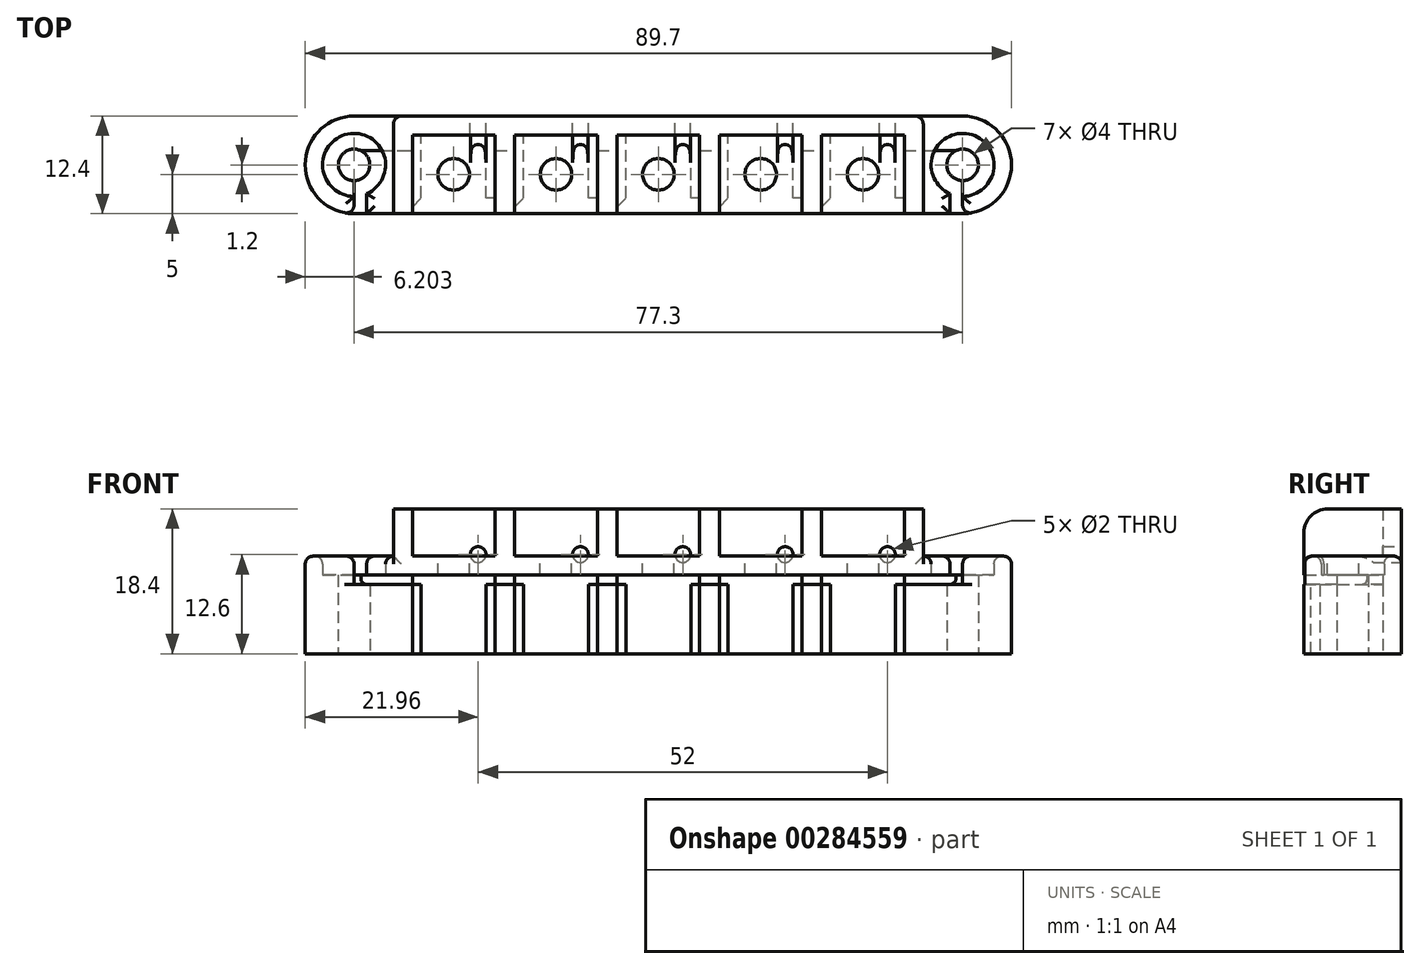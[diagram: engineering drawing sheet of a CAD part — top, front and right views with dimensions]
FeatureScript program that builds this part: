
annotation { "Feature Type Name" : "Feature", "Feature Type Description" : "" }
export const myFeature = defineFeature(function(context is Context, id is Id, definition is map)
    precondition{}
    {
        {
            var Q0;
            Q0=qCreatedBy(makeId("Top.planeOp"),FACE);
            var sketch = newSketch(context, id + "F0", { "sketchPlane" : qUnion([Q0])});
            skLineSegment(sketch, "E0.bottom", {"start": v(-33.77, 0) * mm, "end": v(-23.27, 0) * mm, "construction": true});
            skLineSegment(sketch, "E0.left", {"start": v(-33.77, 0) * mm, "end": v(-33.77, -10) * mm, "construction": true});
            skLineSegment(sketch, "E0.right", {"start": v(-23.27, 0) * mm, "end": v(-23.27, -10) * mm, "construction": true});
            skLineSegment(sketch, "E1.top", {"start": v(-23.27, -10) * mm, "end": v(-20.87, -10) * mm, "construction": true});
            skLineSegment(sketch, "E2.bottom", {"start": v(-36.17, 2.4) * mm, "end": v(31.13, 2.4) * mm, "construction": true});
            skLineSegment(sketch, "E2.left", {"start": v(-36.17, 2.4) * mm, "end": v(-36.17, -10) * mm, "construction": true});
            skArc(sketch, "E3", {"start": v(-41.17, 2.4) * mm, "mid": v(-47.37, -3.8) * mm, "end": v(-41.17, -10) * mm, "construction": true});
            skArc(sketch, "E4", {"start": v(36.13, -10) * mm, "mid": v(42.33, -3.8) * mm, "end": v(36.13, 2.4) * mm, "construction": true});
            skLineSegment(sketch, "E5", {"start": v(-41.17, -10) * mm, "end": v(-36.17, -10) * mm, "construction": true});
            skLineSegment(sketch, "E6", {"start": v(-41.17, 2.4) * mm, "end": v(-36.17, 2.4) * mm, "construction": true});
            skLineSegment(sketch, "E7", {"start": v(-55.27, -5) * mm, "end": v(51.36, -5) * mm, "construction": true});
            skLineSegment(sketch, "E8", {"start": v(-36.17, -10) * mm, "end": v(-33.77, -10) * mm, "construction": true});
            skLineSegment(sketch, "E9.1.0.0", {"start": v(-20.77, 0) * mm, "end": v(-20.77, -10) * mm, "construction": true});
            skLineSegment(sketch, "E9.1.0.1", {"start": v(-20.77, 0) * mm, "end": v(-10.27, 0) * mm, "construction": true});
            skLineSegment(sketch, "E9.1.0.2", {"start": v(-10.27, 0) * mm, "end": v(-10.27, -10) * mm, "construction": true});
            skLineSegment(sketch, "E9.1.0.3", {"start": v(-10.27, -10) * mm, "end": v(-7.87, -10) * mm, "construction": true});
            skLineSegment(sketch, "E9.2.0.0", {"start": v(-7.77, 0) * mm, "end": v(-7.77, -10) * mm, "construction": true});
            skLineSegment(sketch, "E9.2.0.1", {"start": v(-7.77, 0) * mm, "end": v(2.73, 0) * mm, "construction": true});
            skLineSegment(sketch, "E9.2.0.2", {"start": v(2.73, 0) * mm, "end": v(2.73, -10) * mm, "construction": true});
            skLineSegment(sketch, "E9.2.0.3", {"start": v(2.73, -10) * mm, "end": v(5.13, -10) * mm, "construction": true});
            skLineSegment(sketch, "E9.3.0.0", {"start": v(5.23, 0) * mm, "end": v(5.23, -10) * mm, "construction": true});
            skLineSegment(sketch, "E9.3.0.1", {"start": v(5.23, 0) * mm, "end": v(15.73, 0) * mm, "construction": true});
            skLineSegment(sketch, "E9.3.0.2", {"start": v(15.73, 0) * mm, "end": v(15.73, -10) * mm, "construction": true});
            skLineSegment(sketch, "E9.3.0.3", {"start": v(15.73, -10) * mm, "end": v(18.13, -10) * mm, "construction": true});
            skLineSegment(sketch, "E9.4.0.0", {"start": v(18.23, 0) * mm, "end": v(18.23, -10) * mm, "construction": true});
            skLineSegment(sketch, "E9.4.0.1", {"start": v(18.23, 0) * mm, "end": v(28.73, 0) * mm, "construction": true});
            skLineSegment(sketch, "E9.4.0.2", {"start": v(28.73, 0) * mm, "end": v(28.73, -10) * mm, "construction": true});
            skLineSegment(sketch, "E9.4.0.3", {"start": v(28.73, -10) * mm, "end": v(31.13, -10) * mm, "construction": true});
            skLineSegment(sketch, "E9.direction1", {"start": v(-33.77, -10) * mm, "end": v(-20.77, -10) * mm, "construction": true});
            skLineSegment(sketch, "E10", {"start": v(31.13, -10) * mm, "end": v(31.13, 2.4) * mm, "construction": true});
            skLineSegment(sketch, "E11", {"start": v(31.13, 2.4) * mm, "end": v(36.13, 2.4) * mm, "construction": true});
            skLineSegment(sketch, "E12", {"start": v(36.13, -10) * mm, "end": v(31.13, -10) * mm, "construction": true});
            skSolve(sketch);
        }
        {
            var Q0;
            Q0=qCreatedBy(makeId("Top.planeOp"),FACE);
            var sketch = newSketch(context, id + "F1", { "sketchPlane" : qUnion([Q0])});
            skLineSegment(sketch, "E13", {"start": v(-36.17, -10) * mm, "end": v(-33.77, -10) * mm});
            skLineSegment(sketch, "E14", {"start": v(-33.77, -10) * mm, "end": v(-33.77, 0) * mm});
            skLineSegment(sketch, "E15", {"start": v(-33.77, 0) * mm, "end": v(-23.27, 0) * mm});
            skLineSegment(sketch, "E16", {"start": v(-23.27, 0) * mm, "end": v(-23.27, -10) * mm});
            skLineSegment(sketch, "E17.1.0.0", {"start": v(-10.27, 0) * mm, "end": v(-10.27, -10) * mm});
            skLineSegment(sketch, "E17.1.0.1", {"start": v(-20.77, -10) * mm, "end": v(-20.77, 0) * mm});
            skLineSegment(sketch, "E17.1.0.2", {"start": v(-20.77, 0) * mm, "end": v(-10.27, 0) * mm});
            skLineSegment(sketch, "E17.1.0.3", {"start": v(-23.27, -10) * mm, "end": v(-20.77, -10) * mm});
            skLineSegment(sketch, "E17.2.0.0", {"start": v(2.73, 0) * mm, "end": v(2.73, -10) * mm});
            skLineSegment(sketch, "E17.2.0.1", {"start": v(-7.77, -10) * mm, "end": v(-7.77, 0) * mm});
            skLineSegment(sketch, "E17.2.0.2", {"start": v(-7.77, 0) * mm, "end": v(2.73, 0) * mm});
            skLineSegment(sketch, "E17.2.0.3", {"start": v(-10.27, -10) * mm, "end": v(-7.77, -10) * mm});
            skLineSegment(sketch, "E17.3.0.0", {"start": v(15.73, 0) * mm, "end": v(15.73, -10) * mm});
            skLineSegment(sketch, "E17.3.0.1", {"start": v(5.23, -10) * mm, "end": v(5.23, 0) * mm});
            skLineSegment(sketch, "E17.3.0.2", {"start": v(5.23, 0) * mm, "end": v(15.73, 0) * mm});
            skLineSegment(sketch, "E17.3.0.3", {"start": v(2.73, -10) * mm, "end": v(5.23, -10) * mm});
            skLineSegment(sketch, "E17.4.0.0", {"start": v(28.73, 0) * mm, "end": v(28.73, -10) * mm});
            skLineSegment(sketch, "E17.4.0.1", {"start": v(18.23, -10) * mm, "end": v(18.23, 0) * mm});
            skLineSegment(sketch, "E17.4.0.2", {"start": v(18.23, 0) * mm, "end": v(28.73, 0) * mm});
            skLineSegment(sketch, "E17.4.0.3", {"start": v(15.73, -10) * mm, "end": v(18.23, -10) * mm});
            skLineSegment(sketch, "E18", {"start": v(-36.17, -10) * mm, "end": v(-36.17, 2.4) * mm});
            skLineSegment(sketch, "E19", {"start": v(-36.17, 2.4) * mm, "end": v(31.13, 2.4) * mm});
            skLineSegment(sketch, "E20", {"start": v(31.13, 2.4) * mm, "end": v(31.13, -10) * mm});
            skLineSegment(sketch, "E21", {"start": v(31.13, -10) * mm, "end": v(28.73, -10) * mm});
            skSolve(sketch);
        }
        {
            var Q0;
            Q0 = qSketchRegion(id + "F1", true);
            extrude(context, id + "F2", {"entities" : qUnion([Q0]), "depth" : 10 * mm});
        }
        {
            var Q0;
            Q0=qCreatedBy(makeId("Top.planeOp"),FACE);
            var sketch = newSketch(context, id + "F3", { "sketchPlane" : qUnion([Q0])});
            skArc(sketch, "E22", {"start": v(-41.17, 2.4) * mm, "mid": v(-47.37, -3.8) * mm, "end": v(-41.17, -10) * mm});
            skLineSegment(sketch, "E23.bottom", {"start": v(-36.17, 2.4) * mm, "end": v(-41.17, 2.4) * mm});
            skLineSegment(sketch, "E23.top", {"start": v(-36.17, -10) * mm, "end": v(-41.17, -10) * mm});
            skLineSegment(sketch, "E24.bottom", {"start": v(36.13, 2.4) * mm, "end": v(31.13, 2.4) * mm});
            skLineSegment(sketch, "E24.top", {"start": v(36.13, -10) * mm, "end": v(31.13, -10) * mm});
            skLineSegment(sketch, "E24.right", {"start": v(31.13, 2.4) * mm, "end": v(31.13, -10) * mm});
            skArc(sketch, "E25", {"start": v(36.13, -10) * mm, "mid": v(42.33, -3.8) * mm, "end": v(36.13, 2.4) * mm});
            skCircle(sketch, "E26", {"center": v(36.13, -3.8) * mm, "radius": 2 * mm});
            skCircle(sketch, "E27", {"center": v(-41.17, -3.8) * mm, "radius": 2 * mm});
            skLineSegment(sketch, "E28", {"start": v(-36.17, 2.4) * mm, "end": v(-36.17, -10) * mm});
            skSolve(sketch);
        }
        {
            var Q0;
            Q0 = qSketchRegion(id + "F3", true);
            extrude(context, id + "F4", {"entities" : qUnion([Q0]), "operationType" : NewBodyOperationType.ADD, "depth" : 10 * mm});
        }
        {
            var Q0;
            Q0=makeQuery(id+"F2.opExtrude","SWEPT_FACE",FACE,{"disambiguationData":[OSD([sQuery(id+"F1.wireOp",EDGE,"E17.2.0.3")])]});
            var sketch = newSketch(context, id + "F5", { "sketchPlane" : qUnion([Q0])});
            skPoint(sketch, "E29.oppositeSnap0", {"position": v(16.83, 8.8) * mm});
            skLineSegment(sketch, "E29.bottom", {"start": v(-41.17, 10) * mm, "end": v(36.13, 10) * mm});
            skLineSegment(sketch, "E29.top", {"start": v(-41.17, 8.8) * mm, "end": v(36.13, 8.8) * mm});
            skLineSegment(sketch, "E29.left", {"start": v(-41.17, 10) * mm, "end": v(-41.17, 8.8) * mm});
            skLineSegment(sketch, "E29.right", {"start": v(36.13, 10) * mm, "end": v(36.13, 8.8) * mm});
            skSolve(sketch);
        }
        {
            var Q0;
            Q0 = qSketchRegion(id + "F5", true);
            extrude(context, id + "F6", {"entities" : qUnion([Q0]), "operationType" : NewBodyOperationType.REMOVE, "oppositeDirection" : true, "depth" : 8 * mm});
        }
        {
            var Q0;
            Q0=makeQuery(id+"F4.boolean.opBoolean","MERGE",FACE,{"derivedFrom":[makeQuery(id+"FwgUjB52n0EN0py_0.opExtrude","CAP_FACE",FACE,{"disambiguationData":[OSD([sQuery(id+"F1.wireOp",EDGE,"fT5GCNOj-Di1p-hgey-o5If-u0ZHMEbWG8jb.bottom"),sQuery(id+"F1.wireOp",EDGE,"fT5GCNOj-Di1p-hgey-o5If-u0ZHMEbWG8jb.left"),sQuery(id+"F1.wireOp",EDGE,"fT5GCNOj-Di1p-hgey-o5If-u0ZHMEbWG8jb.right"),sQuery(id+"F1.wireOp",EDGE,"4aupWsoh-EStk-4eZo-ruS9-NkXySoXvfakK"),sQuery(id+"F1.wireOp",EDGE,"e8ce3505-5f8b-4699-837b-7b2c080ba128.1.0.0"),sQuery(id+"F1.wireOp",EDGE,"e8ce3505-5f8b-4699-837b-7b2c080ba128.1.0.1"),sQuery(id+"F1.wireOp",EDGE,"e8ce3505-5f8b-4699-837b-7b2c080ba128.1.0.2"),sQuery(id+"F1.wireOp",EDGE,"e8ce3505-5f8b-4699-837b-7b2c080ba128.1.0.3"),sQuery(id+"F1.wireOp",EDGE,"e8ce3505-5f8b-4699-837b-7b2c080ba128.2.0.0"),sQuery(id+"F1.wireOp",EDGE,"e8ce3505-5f8b-4699-837b-7b2c080ba128.2.0.1"),sQuery(id+"F1.wireOp",EDGE,"e8ce3505-5f8b-4699-837b-7b2c080ba128.2.0.2"),sQuery(id+"F1.wireOp",EDGE,"e8ce3505-5f8b-4699-837b-7b2c080ba128.2.0.3"),sQuery(id+"F1.wireOp",EDGE,"e8ce3505-5f8b-4699-837b-7b2c080ba128.3.0.0"),sQuery(id+"F1.wireOp",EDGE,"e8ce3505-5f8b-4699-837b-7b2c080ba128.3.0.1"),sQuery(id+"F1.wireOp",EDGE,"e8ce3505-5f8b-4699-837b-7b2c080ba128.3.0.2"),sQuery(id+"F1.wireOp",EDGE,"e8ce3505-5f8b-4699-837b-7b2c080ba128.3.0.3"),sQuery(id+"F1.wireOp",EDGE,"e8ce3505-5f8b-4699-837b-7b2c080ba128.4.0.0"),sQuery(id+"F1.wireOp",EDGE,"e8ce3505-5f8b-4699-837b-7b2c080ba128.4.0.1"),sQuery(id+"F1.wireOp",EDGE,"e8ce3505-5f8b-4699-837b-7b2c080ba128.4.0.2"),sQuery(id+"F1.wireOp",EDGE,"e8ce3505-5f8b-4699-837b-7b2c080ba128.4.0.3"),sQuery(id+"F1.wireOp",EDGE,"e8ce3505-5f8b-4699-837b-7b2c080ba128.5.0.0"),sQuery(id+"F1.wireOp",EDGE,"e8ce3505-5f8b-4699-837b-7b2c080ba128.5.0.1"),sQuery(id+"F1.wireOp",EDGE,"e8ce3505-5f8b-4699-837b-7b2c080ba128.5.0.2"),sQuery(id+"F1.wireOp",EDGE,"e8ce3505-5f8b-4699-837b-7b2c080ba128.5.0.3"),sQuery(id+"F1.wireOp",EDGE,"WsZVMAvk-gSrm-D8FK-Weo4-wgcM3uc7j39G"),sQuery(id+"F1.wireOp",EDGE,"UKXqcqMu-vQly-xDY7-aWyL-ivSJE3wOXlFD"),sQuery(id+"F1.wireOp",EDGE,"qiBo0CbL-PMXg-gfnk-IXnX-IWupUi0J8d6I"),sQuery(id+"F1.wireOp",EDGE,"uGecGJv5-VCCF-BD4v-ZbDO-07ZKYqrsvqIm")])],"isStart":false}),makeQuery(id+"F4.opExtrude","CAP_FACE",FACE,{"disambiguationData":[OSD([sQuery(id+"F3.wireOp",EDGE,"E22"),sQuery(id+"F3.wireOp",EDGE,"E23.bottom"),sQuery(id+"F3.wireOp",EDGE,"E23.top"),sQuery(id+"F3.wireOp",EDGE,"E27"),sQuery(id+"F3.wireOp",EDGE,"E28")])],"isStart":false}),makeQuery(id+"F4.opExtrude","CAP_FACE",FACE,{"disambiguationData":[OSD([sQuery(id+"F3.wireOp",EDGE,"E24.bottom"),sQuery(id+"F3.wireOp",EDGE,"E24.top"),sQuery(id+"F3.wireOp",EDGE,"E24.right"),sQuery(id+"F3.wireOp",EDGE,"E25"),sQuery(id+"F3.wireOp",EDGE,"E26")])],"isStart":false})]});
            var sketch = newSketch(context, id + "F7", { "sketchPlane" : qUnion([Q0])});
            skLineSegment(sketch, "E30.bottom", {"start": v(-36.17, 2.4) * mm, "end": v(29.83, 2.4) * mm});
            skLineSegment(sketch, "E30.top", {"start": v(-36.17, -10) * mm, "end": v(29.83, -10) * mm});
            skArc(sketch, "E31", {"start": v(-41.17, 2.4) * mm, "mid": v(-47.37, -3.8) * mm, "end": v(-41.17, -10) * mm});
            skLineSegment(sketch, "E32.bottom", {"start": v(-36.17, 2.4) * mm, "end": v(-41.17, 2.4) * mm});
            skLineSegment(sketch, "E32.top", {"start": v(-36.17, -10) * mm, "end": v(-41.17, -10) * mm});
            skArc(sketch, "E33", {"start": v(36.13, -10) * mm, "mid": v(42.33, -3.8) * mm, "end": v(36.13, 2.4) * mm});
            skLineSegment(sketch, "E34.bottom", {"start": v(29.83, 2.4) * mm, "end": v(36.13, 2.4) * mm});
            skLineSegment(sketch, "E34.top", {"start": v(29.83, -10) * mm, "end": v(36.13, -10) * mm});
            skLineSegment(sketch, "E34.right", {"start": v(36.13, 2.4) * mm, "end": v(36.13, -10) * mm});
            skSolve(sketch);
        }
        {
            var Q0;
            Q0 = qSketchRegion(id + "F7", true);
            extrude(context, id + "F8", {"entities" : qUnion([Q0]), "operationType" : NewBodyOperationType.ADD, "depth" : 2.4 * mm});
        }
        {
            var Q0;
            Q0=makeQuery(id+"F8.opExtrude","CAP_FACE",FACE,{"disambiguationData":[OSD([sQuery(id+"F7.wireOp",EDGE,"E30.bottom"),sQuery(id+"F7.wireOp",EDGE,"E30.top"),sQuery(id+"F7.wireOp",EDGE,"E31"),sQuery(id+"F7.wireOp",EDGE,"E32.bottom"),sQuery(id+"F7.wireOp",EDGE,"E32.top"),sQuery(id+"F7.wireOp",EDGE,"E33"),sQuery(id+"F7.wireOp",EDGE,"E34.bottom"),sQuery(id+"F7.wireOp",EDGE,"E34.top")])],"isStart":true});
            var sketch = newSketch(context, id + "F9", { "sketchPlane" : qUnion([Q0])});
            skArc(sketch, "E35", {"start": v(-41.17, 7.8) * mm, "mid": v(-41.98, -0.12) * mm, "end": v(-39.57, 7.47) * mm});
            skArc(sketch, "E36", {"start": v(34.53, 7.47) * mm, "mid": v(36.95, -0.12) * mm, "end": v(36.13, 7.8) * mm});
            skLineSegment(sketch, "E37.bottom", {"start": v(-41.17, 10) * mm, "end": v(-39.57, 10) * mm});
            skLineSegment(sketch, "E37.left", {"start": v(-41.17, 10) * mm, "end": v(-41.17, 7.8) * mm});
            skLineSegment(sketch, "E37.right", {"start": v(-39.57, 10) * mm, "end": v(-39.57, 7.47) * mm});
            skLineSegment(sketch, "E38.bottom", {"start": v(36.13, 10) * mm, "end": v(34.53, 10) * mm});
            skLineSegment(sketch, "E38.left", {"start": v(36.13, 10) * mm, "end": v(36.13, 7.8) * mm});
            skLineSegment(sketch, "E38.right", {"start": v(34.53, 10) * mm, "end": v(34.53, 7.47) * mm});
            skSolve(sketch);
        }
        {
            var Q0;
            Q0 = qSketchRegion(id + "F9", true);
            extrude(context, id + "F10", {"entities" : qUnion([Q0]), "operationType" : NewBodyOperationType.REMOVE, "oppositeDirection" : true, "depth" : 5 * mm});
        }
        {
            var Q0;
            Q0=makeQuery(id+"F8.opExtrude","CAP_FACE",FACE,{"disambiguationData":[OSD([sQuery(id+"F7.wireOp",EDGE,"E30.bottom"),sQuery(id+"F7.wireOp",EDGE,"E30.top"),sQuery(id+"F7.wireOp",EDGE,"E31"),sQuery(id+"F7.wireOp",EDGE,"E32.bottom"),sQuery(id+"F7.wireOp",EDGE,"E32.top"),sQuery(id+"F7.wireOp",EDGE,"E33"),sQuery(id+"F7.wireOp",EDGE,"E34.bottom"),sQuery(id+"F7.wireOp",EDGE,"E34.top")])],"isStart":false});
            var sketch = newSketch(context, id + "F11", { "sketchPlane" : qUnion([Q0])});
            skCircle(sketch, "E39", {"center": v(-28.52, -5) * mm, "radius": 2 * mm});
            skCircle(sketch, "E40.1.0.0", {"center": v(-15.52, -5) * mm, "radius": 2 * mm});
            skCircle(sketch, "E40.2.0.0", {"center": v(-2.52, -5) * mm, "radius": 2 * mm});
            skCircle(sketch, "E40.3.0.0", {"center": v(10.48, -5) * mm, "radius": 2 * mm});
            skCircle(sketch, "E40.4.0.0", {"center": v(23.48, -5) * mm, "radius": 2 * mm});
            skLineSegment(sketch, "E40.direction1", {"start": v(-28.52, -5) * mm, "end": v(-15.52, -5) * mm, "construction": true});
            skSolve(sketch);
        }
        {
            var Q0;
            Q0 = qSketchRegion(id + "F11", true);
            var Q1;
            Q1=makeQuery(id+"F8.opExtrude","CAP_FACE",FACE,{"disambiguationData":[OSD([sQuery(id+"F7.wireOp",EDGE,"E30.bottom"),sQuery(id+"F7.wireOp",EDGE,"E30.top"),sQuery(id+"F7.wireOp",EDGE,"E31"),sQuery(id+"F7.wireOp",EDGE,"E32.bottom"),sQuery(id+"F7.wireOp",EDGE,"E32.top"),sQuery(id+"F7.wireOp",EDGE,"E33"),sQuery(id+"F7.wireOp",EDGE,"E34.bottom"),sQuery(id+"F7.wireOp",EDGE,"E34.top")])],"isStart":true});
            extrude(context, id + "F12", {"entities" : qUnion([Q0]), "operationType" : NewBodyOperationType.REMOVE, "endBound" : BoundingType.UP_TO_SURFACE, "oppositeDirection" : true, "endBoundEntityFace" : qUnion([Q1]), "depth" : 25 * mm});
        }
        {
            var Q0;
            Q0=makeQuery(id+"F8.opExtrude","CAP_FACE",FACE,{"disambiguationData":[OSD([sQuery(id+"F7.wireOp",EDGE,"E30.bottom"),sQuery(id+"F7.wireOp",EDGE,"E30.top"),sQuery(id+"F7.wireOp",EDGE,"E31"),sQuery(id+"F7.wireOp",EDGE,"E32.bottom"),sQuery(id+"F7.wireOp",EDGE,"E32.top"),sQuery(id+"F7.wireOp",EDGE,"E33"),sQuery(id+"F7.wireOp",EDGE,"E34.bottom"),sQuery(id+"F7.wireOp",EDGE,"E34.top")])],"isStart":false});
            var sketch = newSketch(context, id + "F13", { "sketchPlane" : qUnion([Q0])});
            skLineSegment(sketch, "E41.left", {"start": v(-33.77, 0) * mm, "end": v(-33.77, -10) * mm});
            skLineSegment(sketch, "E42", {"start": v(-33.77, -10) * mm, "end": v(-36.17, -10) * mm});
            skLineSegment(sketch, "E43", {"start": v(31.13, 2.4) * mm, "end": v(-36.17, 2.4) * mm});
            skLineSegment(sketch, "E44", {"start": v(-36.17, 2.4) * mm, "end": v(-36.17, -10) * mm});
            skLineSegment(sketch, "E45", {"start": v(-33.77, 0) * mm, "end": v(-23.27, 0) * mm});
            skLineSegment(sketch, "E46", {"start": v(-23.27, 0) * mm, "end": v(-23.27, -10) * mm});
            skLineSegment(sketch, "E47.1.0.0", {"start": v(-20.77, -10) * mm, "end": v(-23.27, -10) * mm});
            skLineSegment(sketch, "E47.1.0.1", {"start": v(-20.77, 0) * mm, "end": v(-20.77, -10) * mm});
            skLineSegment(sketch, "E47.1.0.2", {"start": v(-20.77, 0) * mm, "end": v(-10.27, 0) * mm});
            skLineSegment(sketch, "E47.1.0.3", {"start": v(-10.27, 0) * mm, "end": v(-10.27, -10) * mm});
            skLineSegment(sketch, "E47.2.0.0", {"start": v(-7.77, -10) * mm, "end": v(-10.27, -10) * mm});
            skLineSegment(sketch, "E47.2.0.1", {"start": v(-7.77, 0) * mm, "end": v(-7.77, -10) * mm});
            skLineSegment(sketch, "E47.2.0.2", {"start": v(-7.77, 0) * mm, "end": v(2.73, 0) * mm});
            skLineSegment(sketch, "E47.2.0.3", {"start": v(2.73, 0) * mm, "end": v(2.73, -10) * mm});
            skLineSegment(sketch, "E47.3.0.0", {"start": v(5.23, -10) * mm, "end": v(2.73, -10) * mm});
            skLineSegment(sketch, "E47.3.0.1", {"start": v(5.23, 0) * mm, "end": v(5.23, -10) * mm});
            skLineSegment(sketch, "E47.3.0.2", {"start": v(5.23, 0) * mm, "end": v(15.73, 0) * mm});
            skLineSegment(sketch, "E47.3.0.3", {"start": v(15.73, 0) * mm, "end": v(15.73, -10) * mm});
            skLineSegment(sketch, "E47.4.0.0", {"start": v(18.23, -10) * mm, "end": v(15.73, -10) * mm});
            skLineSegment(sketch, "E47.4.0.1", {"start": v(18.23, 0) * mm, "end": v(18.23, -10) * mm});
            skLineSegment(sketch, "E47.4.0.2", {"start": v(18.23, 0) * mm, "end": v(28.73, 0) * mm});
            skLineSegment(sketch, "E47.4.0.3", {"start": v(28.73, 0) * mm, "end": v(28.73, -10) * mm});
            skLineSegment(sketch, "E48", {"start": v(28.73, -10) * mm, "end": v(31.13, -10) * mm});
            skLineSegment(sketch, "E49", {"start": v(31.13, -10) * mm, "end": v(31.13, 2.4) * mm});
            skSolve(sketch);
        }
        {
            var Q0;
            Q0 = qSketchRegion(id + "F13", true);
            extrude(context, id + "F14", {"entities" : qUnion([Q0]), "operationType" : NewBodyOperationType.ADD, "depth" : 6 * mm});
        }
        {
            var Q0;
            Q0=makeQuery(id+"F8.boolean.opBoolean","MERGE",FACE,{"derivedFrom":[makeQuery(id+"F4.boolean.opBoolean","MERGE",FACE,{"derivedFrom":[makeQuery(id+"FwgUjB52n0EN0py_0.opExtrude","SWEPT_FACE",FACE,{"disambiguationData":[OSD([sQuery(id+"F1.wireOp",EDGE,"qiBo0CbL-PMXg-gfnk-IXnX-IWupUi0J8d6I")])]}),makeQuery(id+"F4.opExtrude","SWEPT_FACE",FACE,{"disambiguationData":[OSD([sQuery(id+"F3.wireOp",EDGE,"E23.bottom")])]}),makeQuery(id+"F4.opExtrude","SWEPT_FACE",FACE,{"disambiguationData":[OSD([sQuery(id+"F3.wireOp",EDGE,"E24.bottom")])]})]}),makeQuery(id+"F8.opExtrude","SWEPT_FACE",FACE,{"disambiguationData":[OSD([sQuery(id+"F7.wireOp",EDGE,"E30.bottom"),sQuery(id+"F7.wireOp",EDGE,"E32.bottom"),sQuery(id+"F7.wireOp",EDGE,"E34.bottom")])]})]});
            var sketch = newSketch(context, id + "F15", { "sketchPlane" : qUnion([Q0])});
            skCircle(sketch, "E50", {"center": v(-26.59, 12.6) * mm, "radius": 1 * mm});
            skCircle(sketch, "E51.1.0.0", {"center": v(-13.59, 12.6) * mm, "radius": 1 * mm});
            skCircle(sketch, "E51.2.0.0", {"center": v(-0.59, 12.6) * mm, "radius": 1 * mm});
            skCircle(sketch, "E51.3.0.0", {"center": v(12.41, 12.6) * mm, "radius": 1 * mm});
            skCircle(sketch, "E51.4.0.0", {"center": v(25.41, 12.6) * mm, "radius": 1 * mm});
            skLineSegment(sketch, "E51.direction1", {"start": v(-26.59, 12.6) * mm, "end": v(43.41, 12.6) * mm, "construction": true});
            skLineSegment(sketch, "E52", {"start": v(-26.59, 20.3) * mm, "end": v(-26.59, -3.8) * mm, "construction": true});
            skSolve(sketch);
        }
        {
            var Q0;
            Q0 = qSketchRegion(id + "F15", true);
            var Q1;
            Q1=makeQuery(id+"F2.opExtrude","SWEPT_FACE",FACE,{"disambiguationData":[OSD([sQuery(id+"F1.wireOp",EDGE,"E15")])]});
            extrude(context, id + "F16", {"entities" : qUnion([Q0]), "operationType" : NewBodyOperationType.REMOVE, "oppositeDirection" : true, "endBoundEntityFace" : qUnion([Q1]), "depth" : 2.9 * mm});
        }
        {
            var Q0;
            {var subQ0=sQuery(id+"F7.wireOp",EDGE,"E34.top");var subQ1=sQuery(id+"F7.wireOp",EDGE,"E32.top");var subQ2=sQuery(id+"F7.wireOp",EDGE,"E30.top");Q0=makeQuery(id+"F16.boolean.opBoolean","INTERSECT",EDGE,{"derivedFrom":[makeQuery(id+"F14.boolean.opBoolean","SPLIT",FACE,{"disambiguationData":[TD([makeQuery(id+"F12.boolean.opBoolean","COPY",FACE,{"derivedFrom":makeQuery(id+"F12.opExtrude","SWEPT_FACE",FACE,{"disambiguationData":[OSD([sQuery(id+"F11.wireOp",EDGE,"E40.4.0.0")])]})})])],"derivedFrom":makeQuery(id+"F8.opExtrude","CAP_FACE",FACE,{"disambiguationData":[OSD([sQuery(id+"F7.wireOp",EDGE,"E30.bottom"),subQ2,sQuery(id+"F7.wireOp",EDGE,"E31"),sQuery(id+"F7.wireOp",EDGE,"E32.bottom"),subQ1,sQuery(id+"F7.wireOp",EDGE,"E33"),sQuery(id+"F7.wireOp",EDGE,"E34.bottom"),subQ0])],"isStart":false})}),makeQuery(id+"F16.opExtrude","CAP_FACE",FACE,{"disambiguationData":[OSD([sQuery(id+"F15.wireOp",EDGE,"E50")])],"isStart":false})]});}
            var Q1;
            {var subQ0=sQuery(id+"F7.wireOp",EDGE,"E34.top");var subQ1=sQuery(id+"F7.wireOp",EDGE,"E32.top");var subQ2=sQuery(id+"F7.wireOp",EDGE,"E30.top");Q1=makeQuery(id+"F16.boolean.opBoolean","INTERSECT",EDGE,{"derivedFrom":[makeQuery(id+"F14.boolean.opBoolean","SPLIT",FACE,{"disambiguationData":[TD([makeQuery(id+"F12.boolean.opBoolean","COPY",FACE,{"derivedFrom":makeQuery(id+"F12.opExtrude","SWEPT_FACE",FACE,{"disambiguationData":[OSD([sQuery(id+"F11.wireOp",EDGE,"E40.3.0.0")])]})})])],"derivedFrom":makeQuery(id+"F8.opExtrude","CAP_FACE",FACE,{"disambiguationData":[OSD([sQuery(id+"F7.wireOp",EDGE,"E30.bottom"),subQ2,sQuery(id+"F7.wireOp",EDGE,"E31"),sQuery(id+"F7.wireOp",EDGE,"E32.bottom"),subQ1,sQuery(id+"F7.wireOp",EDGE,"E33"),sQuery(id+"F7.wireOp",EDGE,"E34.bottom"),subQ0])],"isStart":false})}),makeQuery(id+"F16.opExtrude","CAP_FACE",FACE,{"disambiguationData":[OSD([sQuery(id+"F15.wireOp",EDGE,"E51.1.0.0")])],"isStart":false})]});}
            var Q2;
            {var subQ0=sQuery(id+"F7.wireOp",EDGE,"E34.top");var subQ1=sQuery(id+"F7.wireOp",EDGE,"E32.top");var subQ2=sQuery(id+"F7.wireOp",EDGE,"E30.top");Q2=makeQuery(id+"F16.boolean.opBoolean","INTERSECT",EDGE,{"derivedFrom":[makeQuery(id+"F14.boolean.opBoolean","SPLIT",FACE,{"disambiguationData":[TD([makeQuery(id+"F12.boolean.opBoolean","COPY",FACE,{"derivedFrom":makeQuery(id+"F12.opExtrude","SWEPT_FACE",FACE,{"disambiguationData":[OSD([sQuery(id+"F11.wireOp",EDGE,"E40.2.0.0")])]})})])],"derivedFrom":makeQuery(id+"F8.opExtrude","CAP_FACE",FACE,{"disambiguationData":[OSD([sQuery(id+"F7.wireOp",EDGE,"E30.bottom"),subQ2,sQuery(id+"F7.wireOp",EDGE,"E31"),sQuery(id+"F7.wireOp",EDGE,"E32.bottom"),subQ1,sQuery(id+"F7.wireOp",EDGE,"E33"),sQuery(id+"F7.wireOp",EDGE,"E34.bottom"),subQ0])],"isStart":false})}),makeQuery(id+"F16.opExtrude","CAP_FACE",FACE,{"disambiguationData":[OSD([sQuery(id+"F15.wireOp",EDGE,"E51.2.0.0")])],"isStart":false})]});}
            var Q3;
            {var subQ0=sQuery(id+"F7.wireOp",EDGE,"E34.top");var subQ1=sQuery(id+"F7.wireOp",EDGE,"E32.top");var subQ2=sQuery(id+"F7.wireOp",EDGE,"E30.top");Q3=makeQuery(id+"F16.boolean.opBoolean","INTERSECT",EDGE,{"derivedFrom":[makeQuery(id+"F14.boolean.opBoolean","SPLIT",FACE,{"disambiguationData":[TD([makeQuery(id+"F12.boolean.opBoolean","COPY",FACE,{"derivedFrom":makeQuery(id+"F12.opExtrude","SWEPT_FACE",FACE,{"disambiguationData":[OSD([sQuery(id+"F11.wireOp",EDGE,"E40.1.0.0")])]})})])],"derivedFrom":makeQuery(id+"F8.opExtrude","CAP_FACE",FACE,{"disambiguationData":[OSD([sQuery(id+"F7.wireOp",EDGE,"E30.bottom"),subQ2,sQuery(id+"F7.wireOp",EDGE,"E31"),sQuery(id+"F7.wireOp",EDGE,"E32.bottom"),subQ1,sQuery(id+"F7.wireOp",EDGE,"E33"),sQuery(id+"F7.wireOp",EDGE,"E34.bottom"),subQ0])],"isStart":false})}),makeQuery(id+"F16.opExtrude","CAP_FACE",FACE,{"disambiguationData":[OSD([sQuery(id+"F15.wireOp",EDGE,"E51.3.0.0")])],"isStart":false})]});}
            var Q4;
            {var subQ0=sQuery(id+"F7.wireOp",EDGE,"E34.top");var subQ1=sQuery(id+"F7.wireOp",EDGE,"E32.top");var subQ2=sQuery(id+"F7.wireOp",EDGE,"E30.top");Q4=makeQuery(id+"F16.boolean.opBoolean","INTERSECT",EDGE,{"derivedFrom":[makeQuery(id+"F14.boolean.opBoolean","SPLIT",FACE,{"disambiguationData":[TD([makeQuery(id+"F12.boolean.opBoolean","COPY",FACE,{"derivedFrom":makeQuery(id+"F12.opExtrude","SWEPT_FACE",FACE,{"disambiguationData":[OSD([sQuery(id+"F11.wireOp",EDGE,"E39")])]})})])],"derivedFrom":makeQuery(id+"F8.opExtrude","CAP_FACE",FACE,{"disambiguationData":[OSD([sQuery(id+"F7.wireOp",EDGE,"E30.bottom"),subQ2,sQuery(id+"F7.wireOp",EDGE,"E31"),sQuery(id+"F7.wireOp",EDGE,"E32.bottom"),subQ1,sQuery(id+"F7.wireOp",EDGE,"E33"),sQuery(id+"F7.wireOp",EDGE,"E34.bottom"),subQ0])],"isStart":false})}),makeQuery(id+"F16.opExtrude","CAP_FACE",FACE,{"disambiguationData":[OSD([sQuery(id+"F15.wireOp",EDGE,"E51.4.0.0")])],"isStart":false})]});}
            fillet(context, id + "F17", {"entities" : qUnion([Q0, Q1, Q2, Q3, Q4]), "radius" : 3 * mm, "rho" : 0.5, "crossSection" : FilletCrossSection.CONIC, "allowEdgeOverflow" : false});
        }
        {
            var Q0;
            Q0=makeQuery(id+"F10.boolean.opBoolean","COPY",EDGE,{"derivedFrom":makeQuery(id+"F10.opExtrude","SWEPT_EDGE",EDGE,{"disambiguationData":[OSD([sQuery(id+"F7.wireOp",EDGE,"E30.top"),sQuery(id+"F7.wireOp",EDGE,"E32.top"),sQuery(id+"F7.wireOp",EDGE,"E34.top"),sQuery(id+"F9.wireOp",EDGE,"E37.bottom"),sQuery(id+"F9.wireOp",EDGE,"E37.right")])]})});
            var Q1;
            {var subQ0=sQuery(id+"F5.wireOp",EDGE,"E29.left");Q1=makeQuery(id+"F10.boolean.opBoolean","MERGE",EDGE,{"derivedFrom":[makeQuery(id+"F6.boolean.opBoolean","MERGE",EDGE,{"derivedFrom":[makeQuery(id+"F4.opExtrude","SWEPT_EDGE",EDGE,{"disambiguationData":[OSD([sQuery(id+"F3.wireOp",EDGE,"E22"),sQuery(id+"F3.wireOp",EDGE,"E23.top")])]}),makeQuery(id+"F6.opExtrude","CAP_EDGE",EDGE,{"disambiguationData":[OSD([subQ0])],"isStart":true})]}),makeQuery(id+"F8.opExtrude","SWEPT_EDGE",EDGE,{"disambiguationData":[OSD([sQuery(id+"F5.wireOp",EDGE,"E29.bottom"),subQ0,sQuery(id+"F7.wireOp",EDGE,"E31"),sQuery(id+"F7.wireOp",EDGE,"E32.top")])]}),makeQuery(id+"F10.opExtrude","SWEPT_EDGE",EDGE,{"disambiguationData":[OSD([sQuery(id+"F9.wireOp",EDGE,"E37.bottom"),sQuery(id+"F9.wireOp",EDGE,"E37.left")])]})]});}
            var Q2;
            Q2=makeQuery(id+"F10.boolean.opBoolean","COPY",EDGE,{"derivedFrom":makeQuery(id+"F10.opExtrude","SWEPT_EDGE",EDGE,{"disambiguationData":[OSD([sQuery(id+"F7.wireOp",EDGE,"E30.top"),sQuery(id+"F7.wireOp",EDGE,"E32.top"),sQuery(id+"F7.wireOp",EDGE,"E34.top"),sQuery(id+"F9.wireOp",EDGE,"E38.bottom"),sQuery(id+"F9.wireOp",EDGE,"E38.right")])]})});
            var Q3;
            Q3=makeQuery(id+"F10.boolean.opBoolean","MERGE",EDGE,{"derivedFrom":[makeQuery(id+"F6.boolean.opBoolean","MERGE",EDGE,{"derivedFrom":[makeQuery(id+"F4.opExtrude","SWEPT_EDGE",EDGE,{"disambiguationData":[OSD([sQuery(id+"F3.wireOp",EDGE,"E24.top"),sQuery(id+"F3.wireOp",EDGE,"E25")])]}),makeQuery(id+"F6.opExtrude","CAP_EDGE",EDGE,{"disambiguationData":[OSD([sQuery(id+"F5.wireOp",EDGE,"E29.right")])],"isStart":true})]}),makeQuery(id+"F8.opExtrude","SWEPT_EDGE",EDGE,{"disambiguationData":[OSD([sQuery(id+"F7.wireOp",EDGE,"E33"),sQuery(id+"F7.wireOp",EDGE,"E34.top"),sQuery(id+"F7.wireOp",EDGE,"E34.right")])]}),makeQuery(id+"F10.opExtrude","SWEPT_EDGE",EDGE,{"disambiguationData":[OSD([sQuery(id+"F9.wireOp",EDGE,"E38.bottom"),sQuery(id+"F9.wireOp",EDGE,"E38.left")])]})]});
            var Q4;
            Q4=makeQuery(id+"F8.opExtrude","CAP_EDGE",EDGE,{"disambiguationData":[OSD([sQuery(id+"F7.wireOp",EDGE,"E31")])],"isStart":false});
            var Q5;
            {var subQ1=sQuery(id+"F7.wireOp",EDGE,"E34.bottom");var subQ2=sQuery(id+"F7.wireOp",EDGE,"E32.bottom");var subQ3=sQuery(id+"F7.wireOp",EDGE,"E30.bottom");Q5=makeQuery(id+"F14.boolean.opBoolean","SPLIT",EDGE,{"disambiguationData":[TD([makeQuery(id+"F4.opExtrude","SWEPT_FACE",FACE,{"disambiguationData":[OSD([sQuery(id+"F3.wireOp",EDGE,"E22")])]})])],"derivedFrom":makeQuery(id+"F8.opExtrude","CAP_EDGE",EDGE,{"disambiguationData":[OSD([subQ3,subQ2,subQ1])],"isStart":false})});}
            var Q6;
            Q6=makeQuery(id+"F10.boolean.opBoolean","INTERSECT",EDGE,{"derivedFrom":[makeQuery(id+"F8.opExtrude","CAP_FACE",FACE,{"disambiguationData":[OSD([sQuery(id+"F7.wireOp",EDGE,"E30.bottom"),sQuery(id+"F7.wireOp",EDGE,"E30.top"),sQuery(id+"F7.wireOp",EDGE,"E31"),sQuery(id+"F7.wireOp",EDGE,"E32.bottom"),sQuery(id+"F7.wireOp",EDGE,"E32.top"),sQuery(id+"F7.wireOp",EDGE,"E33"),sQuery(id+"F7.wireOp",EDGE,"E34.bottom"),sQuery(id+"F7.wireOp",EDGE,"E34.top")])],"isStart":false}),makeQuery(id+"F10.opExtrude","SWEPT_FACE",FACE,{"disambiguationData":[OSD([sQuery(id+"F9.wireOp",EDGE,"E35")])]})]});
            var Q7;
            {var subQ0=sQuery(id+"F7.wireOp",EDGE,"E34.top");var subQ1=sQuery(id+"F7.wireOp",EDGE,"E32.top");var subQ2=sQuery(id+"F7.wireOp",EDGE,"E30.top");Q7=makeQuery(id+"F14.boolean.opBoolean","SPLIT",EDGE,{"disambiguationData":[TD([makeQuery(id+"F10.boolean.opBoolean","COPY",FACE,{"derivedFrom":makeQuery(id+"F10.opExtrude","SWEPT_FACE",FACE,{"disambiguationData":[OSD([sQuery(id+"F9.wireOp",EDGE,"E37.right")])]})})])],"derivedFrom":makeQuery(id+"F8.opExtrude","CAP_EDGE",EDGE,{"disambiguationData":[OSD([subQ2,subQ1,subQ0])],"isStart":false})});}
            var Q8;
            Q8=makeQuery(id+"F10.boolean.opBoolean","INTERSECT",EDGE,{"derivedFrom":[makeQuery(id+"F8.opExtrude","CAP_FACE",FACE,{"disambiguationData":[OSD([sQuery(id+"F7.wireOp",EDGE,"E30.bottom"),sQuery(id+"F7.wireOp",EDGE,"E30.top"),sQuery(id+"F7.wireOp",EDGE,"E31"),sQuery(id+"F7.wireOp",EDGE,"E32.bottom"),sQuery(id+"F7.wireOp",EDGE,"E32.top"),sQuery(id+"F7.wireOp",EDGE,"E33"),sQuery(id+"F7.wireOp",EDGE,"E34.bottom"),sQuery(id+"F7.wireOp",EDGE,"E34.top")])],"isStart":false}),makeQuery(id+"F10.opExtrude","SWEPT_FACE",FACE,{"disambiguationData":[OSD([sQuery(id+"F9.wireOp",EDGE,"E37.right")])]})]});
            var Q9;
            Q9=makeQuery(id+"F8.opExtrude","CAP_EDGE",EDGE,{"disambiguationData":[OSD([sQuery(id+"F7.wireOp",EDGE,"E33")])],"isStart":false});
            var Q10;
            {var subQ0=sQuery(id+"F7.wireOp",EDGE,"E34.bottom");var subQ2=sQuery(id+"F7.wireOp",EDGE,"E32.bottom");var subQ3=sQuery(id+"F7.wireOp",EDGE,"E30.bottom");Q10=makeQuery(id+"F14.boolean.opBoolean","SPLIT",EDGE,{"disambiguationData":[TD([makeQuery(id+"F4.opExtrude","SWEPT_FACE",FACE,{"disambiguationData":[OSD([sQuery(id+"F3.wireOp",EDGE,"E25")])]})])],"derivedFrom":makeQuery(id+"F8.opExtrude","CAP_EDGE",EDGE,{"disambiguationData":[OSD([subQ3,subQ2,subQ0])],"isStart":false})});}
            var Q11;
            Q11=makeQuery(id+"F10.boolean.opBoolean","INTERSECT",EDGE,{"derivedFrom":[makeQuery(id+"F8.opExtrude","CAP_FACE",FACE,{"disambiguationData":[OSD([sQuery(id+"F7.wireOp",EDGE,"E30.bottom"),sQuery(id+"F7.wireOp",EDGE,"E30.top"),sQuery(id+"F7.wireOp",EDGE,"E31"),sQuery(id+"F7.wireOp",EDGE,"E32.bottom"),sQuery(id+"F7.wireOp",EDGE,"E32.top"),sQuery(id+"F7.wireOp",EDGE,"E33"),sQuery(id+"F7.wireOp",EDGE,"E34.bottom"),sQuery(id+"F7.wireOp",EDGE,"E34.top")])],"isStart":false}),makeQuery(id+"F10.opExtrude","SWEPT_FACE",FACE,{"disambiguationData":[OSD([sQuery(id+"F9.wireOp",EDGE,"E36")])]})]});
            var Q12;
            {var subQ0=sQuery(id+"F7.wireOp",EDGE,"E34.top");var subQ1=sQuery(id+"F7.wireOp",EDGE,"E32.top");var subQ2=sQuery(id+"F7.wireOp",EDGE,"E30.top");Q12=makeQuery(id+"F14.boolean.opBoolean","SPLIT",EDGE,{"disambiguationData":[TD([makeQuery(id+"F10.boolean.opBoolean","COPY",FACE,{"derivedFrom":makeQuery(id+"F10.opExtrude","SWEPT_FACE",FACE,{"disambiguationData":[OSD([sQuery(id+"F9.wireOp",EDGE,"E38.right")])]})})])],"derivedFrom":makeQuery(id+"F8.opExtrude","CAP_EDGE",EDGE,{"disambiguationData":[OSD([subQ2,subQ1,subQ0])],"isStart":false})});}
            var Q13;
            Q13=makeQuery(id+"F10.boolean.opBoolean","INTERSECT",EDGE,{"derivedFrom":[makeQuery(id+"F8.opExtrude","CAP_FACE",FACE,{"disambiguationData":[OSD([sQuery(id+"F7.wireOp",EDGE,"E30.bottom"),sQuery(id+"F7.wireOp",EDGE,"E30.top"),sQuery(id+"F7.wireOp",EDGE,"E31"),sQuery(id+"F7.wireOp",EDGE,"E32.bottom"),sQuery(id+"F7.wireOp",EDGE,"E32.top"),sQuery(id+"F7.wireOp",EDGE,"E33"),sQuery(id+"F7.wireOp",EDGE,"E34.bottom"),sQuery(id+"F7.wireOp",EDGE,"E34.top")])],"isStart":false}),makeQuery(id+"F10.opExtrude","SWEPT_FACE",FACE,{"disambiguationData":[OSD([sQuery(id+"F9.wireOp",EDGE,"E38.right")])]})]});
            var Q14;
            Q14=makeQuery(id+"F10.boolean.opBoolean","INTERSECT",EDGE,{"derivedFrom":[makeQuery(id+"F8.opExtrude","CAP_FACE",FACE,{"disambiguationData":[OSD([sQuery(id+"F7.wireOp",EDGE,"E30.bottom"),sQuery(id+"F7.wireOp",EDGE,"E30.top"),sQuery(id+"F7.wireOp",EDGE,"E31"),sQuery(id+"F7.wireOp",EDGE,"E32.bottom"),sQuery(id+"F7.wireOp",EDGE,"E32.top"),sQuery(id+"F7.wireOp",EDGE,"E33"),sQuery(id+"F7.wireOp",EDGE,"E34.bottom"),sQuery(id+"F7.wireOp",EDGE,"E34.top")])],"isStart":false}),makeQuery(id+"F10.opExtrude","SWEPT_FACE",FACE,{"disambiguationData":[OSD([sQuery(id+"F9.wireOp",EDGE,"E38.left")])]})]});
            var Q15;
            Q15=makeQuery(id+"F10.boolean.opBoolean","INTERSECT",EDGE,{"derivedFrom":[makeQuery(id+"F8.opExtrude","CAP_FACE",FACE,{"disambiguationData":[OSD([sQuery(id+"F7.wireOp",EDGE,"E30.bottom"),sQuery(id+"F7.wireOp",EDGE,"E30.top"),sQuery(id+"F7.wireOp",EDGE,"E31"),sQuery(id+"F7.wireOp",EDGE,"E32.bottom"),sQuery(id+"F7.wireOp",EDGE,"E32.top"),sQuery(id+"F7.wireOp",EDGE,"E33"),sQuery(id+"F7.wireOp",EDGE,"E34.bottom"),sQuery(id+"F7.wireOp",EDGE,"E34.top")])],"isStart":false}),makeQuery(id+"F10.opExtrude","SWEPT_FACE",FACE,{"disambiguationData":[OSD([sQuery(id+"F9.wireOp",EDGE,"E37.left")])]})]});
            var Q16;
            Q16=makeQuery(id+"F16.boolean.opBoolean","COPY",EDGE,{"derivedFrom":makeQuery(id+"F16.opExtrude","CAP_EDGE",EDGE,{"disambiguationData":[OSD([sQuery(id+"F15.wireOp",EDGE,"E51.4.0.0")])],"isStart":true})});
            var Q17;
            Q17=makeQuery(id+"F16.boolean.opBoolean","COPY",EDGE,{"derivedFrom":makeQuery(id+"F16.opExtrude","CAP_EDGE",EDGE,{"disambiguationData":[OSD([sQuery(id+"F15.wireOp",EDGE,"E51.3.0.0")])],"isStart":true})});
            var Q18;
            Q18=makeQuery(id+"F16.boolean.opBoolean","COPY",EDGE,{"derivedFrom":makeQuery(id+"F16.opExtrude","CAP_EDGE",EDGE,{"disambiguationData":[OSD([sQuery(id+"F15.wireOp",EDGE,"E51.2.0.0")])],"isStart":true})});
            var Q19;
            Q19=makeQuery(id+"F16.boolean.opBoolean","COPY",EDGE,{"derivedFrom":makeQuery(id+"F16.opExtrude","CAP_EDGE",EDGE,{"disambiguationData":[OSD([sQuery(id+"F15.wireOp",EDGE,"E51.1.0.0")])],"isStart":true})});
            var Q20;
            Q20=makeQuery(id+"F16.boolean.opBoolean","COPY",EDGE,{"derivedFrom":makeQuery(id+"F16.opExtrude","CAP_EDGE",EDGE,{"disambiguationData":[OSD([sQuery(id+"F15.wireOp",EDGE,"E50")])],"isStart":true})});
            var Q21;
            Q21=makeQuery(id+"F14.opExtrude","SWEPT_EDGE",EDGE,{"disambiguationData":[OSD([sQuery(id+"F7.wireOp",EDGE,"E30.bottom"),sQuery(id+"F7.wireOp",EDGE,"E32.bottom"),sQuery(id+"F7.wireOp",EDGE,"E34.bottom"),sQuery(id+"F13.wireOp",EDGE,"E43"),sQuery(id+"F13.wireOp",EDGE,"E49")])]});
            var Q22;
            Q22=makeQuery(id+"F14.opExtrude","SWEPT_EDGE",EDGE,{"disambiguationData":[OSD([sQuery(id+"F7.wireOp",EDGE,"E30.bottom"),sQuery(id+"F7.wireOp",EDGE,"E32.bottom"),sQuery(id+"F7.wireOp",EDGE,"E34.bottom"),sQuery(id+"F13.wireOp",EDGE,"E43"),sQuery(id+"F13.wireOp",EDGE,"E44")])]});
            fillet(context, id + "F18", {"entities" : qUnion([Q0, Q1, Q2, Q3, Q4, Q5, Q6, Q7, Q8, Q9, Q10, Q11, Q12, Q13, Q14, Q15, Q16, Q17, Q18, Q19, Q20, Q21, Q22]), "radius" : 1 * mm, "tangentPropagation" : true, "allowEdgeOverflow" : false});
        }
        {
            var Q0;
            {var subQ1=sQuery(id+"F1.wireOp",EDGE,"E17.1.0.0");var subQ2=sQuery(id+"F5.wireOp",EDGE,"E29.bottom");Q0=makeQuery(id+"F6.boolean.opBoolean","COPY",EDGE,{"disambiguationData":[TD([makeQuery(id+"F2.opExtrude","SWEPT_FACE",FACE,{"disambiguationData":[OSD([subQ1])]})])],"derivedFrom":makeQuery(id+"F6.opExtrude","CAP_EDGE",EDGE,{"disambiguationData":[OSD([subQ2])],"isStart":false})});}
            var Q1;
            {var subQ0=sQuery(id+"F5.wireOp",EDGE,"E29.top");Q1=makeQuery(id+"F6.boolean.opBoolean","COPY",EDGE,{"disambiguationData":[TD([makeQuery(id+"F2.opExtrude","SWEPT_FACE",FACE,{"disambiguationData":[OSD([sQuery(id+"F1.wireOp",EDGE,"E17.1.0.0")])]})])],"derivedFrom":makeQuery(id+"F6.opExtrude","CAP_EDGE",EDGE,{"disambiguationData":[OSD([subQ0])],"isStart":false})});}
            var Q2;
            {var subQ0=sQuery(id+"F5.wireOp",EDGE,"E29.top");Q2=makeQuery(id+"F6.boolean.opBoolean","COPY",EDGE,{"disambiguationData":[TD([makeQuery(id+"F2.opExtrude","SWEPT_FACE",FACE,{"disambiguationData":[OSD([sQuery(id+"F1.wireOp",EDGE,"E16")])]})])],"derivedFrom":makeQuery(id+"F6.opExtrude","CAP_EDGE",EDGE,{"disambiguationData":[OSD([subQ0])],"isStart":false})});}
            var Q3;
            {var subQ0=sQuery(id+"F1.wireOp",EDGE,"E16");var subQ2=sQuery(id+"F5.wireOp",EDGE,"E29.bottom");Q3=makeQuery(id+"F6.boolean.opBoolean","COPY",EDGE,{"disambiguationData":[TD([makeQuery(id+"F2.opExtrude","SWEPT_FACE",FACE,{"disambiguationData":[OSD([subQ0])]})])],"derivedFrom":makeQuery(id+"F6.opExtrude","CAP_EDGE",EDGE,{"disambiguationData":[OSD([subQ2])],"isStart":false})});}
            var Q4;
            {var subQ0=sQuery(id+"F5.wireOp",EDGE,"E29.top");Q4=makeQuery(id+"F6.boolean.opBoolean","COPY",EDGE,{"disambiguationData":[TD([makeQuery(id+"F2.opExtrude","SWEPT_FACE",FACE,{"disambiguationData":[OSD([sQuery(id+"F1.wireOp",EDGE,"E17.2.0.0")])]})])],"derivedFrom":makeQuery(id+"F6.opExtrude","CAP_EDGE",EDGE,{"disambiguationData":[OSD([subQ0])],"isStart":false})});}
            var Q5;
            {var subQ1=sQuery(id+"F1.wireOp",EDGE,"E17.2.0.0");var subQ2=sQuery(id+"F5.wireOp",EDGE,"E29.bottom");Q5=makeQuery(id+"F6.boolean.opBoolean","COPY",EDGE,{"disambiguationData":[TD([makeQuery(id+"F2.opExtrude","SWEPT_FACE",FACE,{"disambiguationData":[OSD([subQ1])]})])],"derivedFrom":makeQuery(id+"F6.opExtrude","CAP_EDGE",EDGE,{"disambiguationData":[OSD([subQ2])],"isStart":false})});}
            var Q6;
            {var subQ0=sQuery(id+"F1.wireOp",EDGE,"E17.3.0.0");var subQ2=sQuery(id+"F5.wireOp",EDGE,"E29.bottom");Q6=makeQuery(id+"F6.boolean.opBoolean","COPY",EDGE,{"disambiguationData":[TD([makeQuery(id+"F2.opExtrude","SWEPT_FACE",FACE,{"disambiguationData":[OSD([subQ0])]})])],"derivedFrom":makeQuery(id+"F6.opExtrude","CAP_EDGE",EDGE,{"disambiguationData":[OSD([subQ2])],"isStart":false})});}
            var Q7;
            {var subQ0=sQuery(id+"F5.wireOp",EDGE,"E29.top");Q7=makeQuery(id+"F6.boolean.opBoolean","COPY",EDGE,{"disambiguationData":[TD([makeQuery(id+"F2.opExtrude","SWEPT_FACE",FACE,{"disambiguationData":[OSD([sQuery(id+"F1.wireOp",EDGE,"E17.3.0.0")])]})])],"derivedFrom":makeQuery(id+"F6.opExtrude","CAP_EDGE",EDGE,{"disambiguationData":[OSD([subQ0])],"isStart":false})});}
            var Q8;
            {var subQ0=sQuery(id+"F5.wireOp",EDGE,"E29.top");Q8=makeQuery(id+"F6.boolean.opBoolean","COPY",EDGE,{"disambiguationData":[TD([makeQuery(id+"F2.opExtrude","SWEPT_FACE",FACE,{"disambiguationData":[OSD([sQuery(id+"F1.wireOp",EDGE,"E17.4.0.0")])]})])],"derivedFrom":makeQuery(id+"F6.opExtrude","CAP_EDGE",EDGE,{"disambiguationData":[OSD([subQ0])],"isStart":false})});}
            var Q9;
            {var subQ3=sQuery(id+"F1.wireOp",EDGE,"E17.4.0.0");var subQ4=makeQuery(id+"F2.opExtrude","SWEPT_FACE",FACE,{"disambiguationData":[OSD([subQ3])]});var subQ8=sQuery(id+"F5.wireOp",EDGE,"E29.bottom");Q9=makeQuery(id+"F10.boolean.opBoolean","SPLIT",EDGE,{"disambiguationData":[topologyDisambiguationEdgeConnected([makeQuery(id+"F8.opExtrude","CAP_FACE",FACE,{"disambiguationData":[OSD([sQuery(id+"F7.wireOp",EDGE,"E30.bottom"),sQuery(id+"F7.wireOp",EDGE,"E30.top"),sQuery(id+"F7.wireOp",EDGE,"E31"),sQuery(id+"F7.wireOp",EDGE,"E32.bottom"),sQuery(id+"F7.wireOp",EDGE,"E32.top"),sQuery(id+"F7.wireOp",EDGE,"E33"),sQuery(id+"F7.wireOp",EDGE,"E34.bottom"),sQuery(id+"F7.wireOp",EDGE,"E34.top")])],"isStart":true})])],"derivedFrom":makeQuery(id+"F6.boolean.opBoolean","COPY",EDGE,{"disambiguationData":[TD([subQ4])],"derivedFrom":makeQuery(id+"F6.opExtrude","CAP_EDGE",EDGE,{"disambiguationData":[OSD([subQ8])],"isStart":false})})});}
            var Q10;
            {var subQ0=sQuery(id+"F5.wireOp",EDGE,"E29.top");Q10=makeQuery(id+"F6.boolean.opBoolean","COPY",EDGE,{"disambiguationData":[TD([makeQuery(id+"F2.opExtrude","SWEPT_FACE",FACE,{"disambiguationData":[OSD([sQuery(id+"F1.wireOp",EDGE,"E14")])]})])],"derivedFrom":makeQuery(id+"F6.opExtrude","CAP_EDGE",EDGE,{"disambiguationData":[OSD([subQ0])],"isStart":false})});}
            var Q11;
            {var subQ3=sQuery(id+"F1.wireOp",EDGE,"E14");var subQ4=makeQuery(id+"F2.opExtrude","SWEPT_FACE",FACE,{"disambiguationData":[OSD([subQ3])]});var subQ8=sQuery(id+"F5.wireOp",EDGE,"E29.bottom");Q11=makeQuery(id+"F10.boolean.opBoolean","SPLIT",EDGE,{"disambiguationData":[topologyDisambiguationEdgeConnected([makeQuery(id+"F8.opExtrude","CAP_FACE",FACE,{"disambiguationData":[OSD([sQuery(id+"F7.wireOp",EDGE,"E30.bottom"),sQuery(id+"F7.wireOp",EDGE,"E30.top"),sQuery(id+"F7.wireOp",EDGE,"E31"),sQuery(id+"F7.wireOp",EDGE,"E32.bottom"),sQuery(id+"F7.wireOp",EDGE,"E32.top"),sQuery(id+"F7.wireOp",EDGE,"E33"),sQuery(id+"F7.wireOp",EDGE,"E34.bottom"),sQuery(id+"F7.wireOp",EDGE,"E34.top")])],"isStart":true})])],"derivedFrom":makeQuery(id+"F6.boolean.opBoolean","COPY",EDGE,{"disambiguationData":[TD([subQ4])],"derivedFrom":makeQuery(id+"F6.opExtrude","CAP_EDGE",EDGE,{"disambiguationData":[OSD([subQ8])],"isStart":false})})});}
            fillet(context, id + "F19", {"entities" : qUnion([Q0, Q1, Q2, Q3, Q4, Q5, Q6, Q7, Q8, Q9, Q10, Q11]), "radius" : .6 * mm, "tangentPropagation" : true, "allowEdgeOverflow" : false});
        }
        {
            var Q0;
            Q0=makeQuery(id+"F14.opExtrude","CAP_EDGE",EDGE,{"disambiguationData":[OSD([sQuery(id+"F13.wireOp",EDGE,"E48")])],"isStart":false});
            var Q1;
            Q1=makeQuery(id+"F14.opExtrude","CAP_EDGE",EDGE,{"disambiguationData":[OSD([sQuery(id+"F13.wireOp",EDGE,"E47.4.0.0")])],"isStart":false});
            var Q2;
            Q2=makeQuery(id+"F14.opExtrude","CAP_EDGE",EDGE,{"disambiguationData":[OSD([sQuery(id+"F13.wireOp",EDGE,"E47.3.0.0")])],"isStart":false});
            var Q3;
            Q3=makeQuery(id+"F14.opExtrude","CAP_EDGE",EDGE,{"disambiguationData":[OSD([sQuery(id+"F13.wireOp",EDGE,"E47.2.0.0")])],"isStart":false});
            var Q4;
            Q4=makeQuery(id+"F14.opExtrude","CAP_EDGE",EDGE,{"disambiguationData":[OSD([sQuery(id+"F13.wireOp",EDGE,"E47.1.0.0")])],"isStart":false});
            var Q5;
            Q5=makeQuery(id+"F14.opExtrude","CAP_EDGE",EDGE,{"disambiguationData":[OSD([sQuery(id+"F13.wireOp",EDGE,"E42")])],"isStart":false});
            fillet(context, id + "F20", {"entities" : qUnion([Q0, Q1, Q2, Q3, Q4, Q5]), "radius" : 3 * mm, "tangentPropagation" : true, "allowEdgeOverflow" : false});
        }
        {
            var Q0;
            Q0=makeQuery(id+"F4.boolean.opBoolean","MERGE",FACE,{"derivedFrom":[makeQuery(id+"F2.opExtrude","CAP_FACE",FACE,{"disambiguationData":[OSD([sQuery(id+"F1.wireOp",EDGE,"E13"),sQuery(id+"F1.wireOp",EDGE,"E14"),sQuery(id+"F1.wireOp",EDGE,"E15"),sQuery(id+"F1.wireOp",EDGE,"E16"),sQuery(id+"F1.wireOp",EDGE,"E17.1.0.0"),sQuery(id+"F1.wireOp",EDGE,"E17.1.0.1"),sQuery(id+"F1.wireOp",EDGE,"E17.1.0.2"),sQuery(id+"F1.wireOp",EDGE,"E17.1.0.3"),sQuery(id+"F1.wireOp",EDGE,"E17.2.0.0"),sQuery(id+"F1.wireOp",EDGE,"E17.2.0.1"),sQuery(id+"F1.wireOp",EDGE,"E17.2.0.2"),sQuery(id+"F1.wireOp",EDGE,"E17.2.0.3"),sQuery(id+"F1.wireOp",EDGE,"E17.3.0.0"),sQuery(id+"F1.wireOp",EDGE,"E17.3.0.1"),sQuery(id+"F1.wireOp",EDGE,"E17.3.0.2"),sQuery(id+"F1.wireOp",EDGE,"E17.3.0.3"),sQuery(id+"F1.wireOp",EDGE,"E17.4.0.0"),sQuery(id+"F1.wireOp",EDGE,"E17.4.0.1"),sQuery(id+"F1.wireOp",EDGE,"E17.4.0.2"),sQuery(id+"F1.wireOp",EDGE,"E17.4.0.3"),sQuery(id+"F1.wireOp",EDGE,"E18"),sQuery(id+"F1.wireOp",EDGE,"E19"),sQuery(id+"F1.wireOp",EDGE,"E20"),sQuery(id+"F1.wireOp",EDGE,"E21")])],"isStart":true}),makeQuery(id+"F4.opExtrude","CAP_FACE",FACE,{"disambiguationData":[OSD([sQuery(id+"F3.wireOp",EDGE,"E22"),sQuery(id+"F3.wireOp",EDGE,"E23.bottom"),sQuery(id+"F3.wireOp",EDGE,"E23.top"),sQuery(id+"F3.wireOp",EDGE,"E27"),sQuery(id+"F3.wireOp",EDGE,"E28")])],"isStart":true}),makeQuery(id+"F4.opExtrude","CAP_FACE",FACE,{"disambiguationData":[OSD([sQuery(id+"F3.wireOp",EDGE,"E24.bottom"),sQuery(id+"F3.wireOp",EDGE,"E24.top"),sQuery(id+"F3.wireOp",EDGE,"E24.right"),sQuery(id+"F3.wireOp",EDGE,"E25"),sQuery(id+"F3.wireOp",EDGE,"E26")])],"isStart":true})]});
            var sketch = newSketch(context, id + "F21", { "sketchPlane" : qUnion([Q0])});
            skLineSegment(sketch, "E53.bottom", {"start": v(28.73, 8) * mm, "end": v(27.6, 8) * mm});
            skLineSegment(sketch, "E53.top", {"start": v(28.73, 0) * mm, "end": v(27.6, 0) * mm});
            skLineSegment(sketch, "E53.left", {"start": v(28.73, 8) * mm, "end": v(28.73, 0) * mm});
            skLineSegment(sketch, "E53.right", {"start": v(27.6, 8) * mm, "end": v(27.6, 0) * mm});
            skLineSegment(sketch, "E54.bottom", {"start": v(18.23, 8) * mm, "end": v(19.36, 8) * mm});
            skLineSegment(sketch, "E54.top", {"start": v(18.23, 0) * mm, "end": v(19.36, 0) * mm});
            skLineSegment(sketch, "E54.left", {"start": v(18.23, 8) * mm, "end": v(18.23, 0) * mm});
            skLineSegment(sketch, "E54.right", {"start": v(19.36, 8) * mm, "end": v(19.36, 0) * mm});
            skLineSegment(sketch, "E55.1.0.0", {"start": v(6.36, 8) * mm, "end": v(6.36, 0) * mm});
            skLineSegment(sketch, "E55.1.0.1", {"start": v(15.73, 8) * mm, "end": v(15.73, 0) * mm});
            skLineSegment(sketch, "E55.1.0.2", {"start": v(15.73, 0) * mm, "end": v(14.6, 0) * mm});
            skLineSegment(sketch, "E55.1.0.3", {"start": v(14.6, 8) * mm, "end": v(14.6, 0) * mm});
            skLineSegment(sketch, "E55.1.0.4", {"start": v(15.73, 8) * mm, "end": v(14.6, 8) * mm});
            skLineSegment(sketch, "E55.1.0.5", {"start": v(5.23, 8) * mm, "end": v(6.36, 8) * mm});
            skLineSegment(sketch, "E55.1.0.6", {"start": v(5.23, 8) * mm, "end": v(5.23, 0) * mm});
            skLineSegment(sketch, "E55.1.0.7", {"start": v(5.23, 0) * mm, "end": v(6.36, 0) * mm});
            skLineSegment(sketch, "E55.2.0.0", {"start": v(-6.64, 8) * mm, "end": v(-6.64, 0) * mm});
            skLineSegment(sketch, "E55.2.0.1", {"start": v(2.73, 8) * mm, "end": v(2.73, 0) * mm});
            skLineSegment(sketch, "E55.2.0.2", {"start": v(2.73, 0) * mm, "end": v(1.6, 0) * mm});
            skLineSegment(sketch, "E55.2.0.3", {"start": v(1.6, 8) * mm, "end": v(1.6, 0) * mm});
            skLineSegment(sketch, "E55.2.0.4", {"start": v(2.73, 8) * mm, "end": v(1.6, 8) * mm});
            skLineSegment(sketch, "E55.2.0.5", {"start": v(-7.77, 8) * mm, "end": v(-6.64, 8) * mm});
            skLineSegment(sketch, "E55.2.0.6", {"start": v(-7.77, 8) * mm, "end": v(-7.77, 0) * mm});
            skLineSegment(sketch, "E55.2.0.7", {"start": v(-7.77, 0) * mm, "end": v(-6.64, 0) * mm});
            skLineSegment(sketch, "E55.3.0.0", {"start": v(-19.64, 8) * mm, "end": v(-19.64, 0) * mm});
            skLineSegment(sketch, "E55.3.0.1", {"start": v(-10.27, 8) * mm, "end": v(-10.27, 0) * mm});
            skLineSegment(sketch, "E55.3.0.2", {"start": v(-10.27, 0) * mm, "end": v(-11.4, 0) * mm});
            skLineSegment(sketch, "E55.3.0.3", {"start": v(-11.4, 8) * mm, "end": v(-11.4, 0) * mm});
            skLineSegment(sketch, "E55.3.0.4", {"start": v(-10.27, 8) * mm, "end": v(-11.4, 8) * mm});
            skLineSegment(sketch, "E55.3.0.5", {"start": v(-20.77, 8) * mm, "end": v(-19.64, 8) * mm});
            skLineSegment(sketch, "E55.3.0.6", {"start": v(-20.77, 8) * mm, "end": v(-20.77, 0) * mm});
            skLineSegment(sketch, "E55.3.0.7", {"start": v(-20.77, 0) * mm, "end": v(-19.64, 0) * mm});
            skLineSegment(sketch, "E55.4.0.0", {"start": v(-32.64, 8) * mm, "end": v(-32.64, 0) * mm});
            skLineSegment(sketch, "E55.4.0.1", {"start": v(-23.27, 8) * mm, "end": v(-23.27, 0) * mm});
            skLineSegment(sketch, "E55.4.0.2", {"start": v(-23.27, 0) * mm, "end": v(-24.4, 0) * mm});
            skLineSegment(sketch, "E55.4.0.3", {"start": v(-24.4, 8) * mm, "end": v(-24.4, 0) * mm});
            skLineSegment(sketch, "E55.4.0.4", {"start": v(-23.27, 8) * mm, "end": v(-24.4, 8) * mm});
            skLineSegment(sketch, "E55.4.0.5", {"start": v(-33.77, 8) * mm, "end": v(-32.64, 8) * mm});
            skLineSegment(sketch, "E55.4.0.6", {"start": v(-33.77, 8) * mm, "end": v(-33.77, 0) * mm});
            skLineSegment(sketch, "E55.4.0.7", {"start": v(-33.77, 0) * mm, "end": v(-32.64, 0) * mm});
            skLineSegment(sketch, "E55.direction1", {"start": v(19.36, 0) * mm, "end": v(6.36, 0) * mm, "construction": true});
            skSolve(sketch);
        }
        {
            var Q0;
            Q0 = qSketchRegion(id + "F21", true);
            var Q1;
            Q1=makeQuery(id+"F8.opExtrude","CAP_FACE",FACE,{"disambiguationData":[OSD([sQuery(id+"F7.wireOp",EDGE,"E30.bottom"),sQuery(id+"F7.wireOp",EDGE,"E30.top"),sQuery(id+"F7.wireOp",EDGE,"E31"),sQuery(id+"F7.wireOp",EDGE,"E32.bottom"),sQuery(id+"F7.wireOp",EDGE,"E32.top"),sQuery(id+"F7.wireOp",EDGE,"E33"),sQuery(id+"F7.wireOp",EDGE,"E34.bottom"),sQuery(id+"F7.wireOp",EDGE,"E34.top")])],"isStart":true});
            extrude(context, id + "F22", {"entities" : qUnion([Q0]), "operationType" : NewBodyOperationType.ADD, "oppositeDirection" : true, "endBoundEntityFace" : qUnion([Q1]), "depth" : 8.8 * mm});
        }
        {
            var Q0;
            {var subQ0=sQuery(id+"F1.wireOp",EDGE,"E17.4.0.1");var subQ1=sQuery(id+"F21.wireOp",EDGE,"E54.bottom");Q0=makeQuery(id+"F22.boolean.opBoolean","SPLIT",EDGE,{"disambiguationData":[topologyDisambiguationEdgeConnected([makeQuery(id+"F2.opExtrude","SWEPT_FACE",FACE,{"disambiguationData":[OSD([subQ0])]})])],"derivedFrom":makeQuery(id+"F22.opExtrude","SWEPT_EDGE",EDGE,{"disambiguationData":[OSD([subQ0,subQ1,sQuery(id+"F21.wireOp",EDGE,"E54.left")])]})});}
            var Q1;
            {var subQ0=sQuery(id+"F1.wireOp",EDGE,"E17.4.0.0");var subQ1=sQuery(id+"F21.wireOp",EDGE,"E53.bottom");Q1=makeQuery(id+"F22.boolean.opBoolean","SPLIT",EDGE,{"disambiguationData":[topologyDisambiguationEdgeConnected([makeQuery(id+"F2.opExtrude","SWEPT_FACE",FACE,{"disambiguationData":[OSD([subQ0])]})])],"derivedFrom":makeQuery(id+"F22.opExtrude","SWEPT_EDGE",EDGE,{"disambiguationData":[OSD([subQ0,subQ1,sQuery(id+"F21.wireOp",EDGE,"E53.left")])]})});}
            var Q2;
            {var subQ0=sQuery(id+"F1.wireOp",EDGE,"E17.3.0.0");var subQ1=sQuery(id+"F21.wireOp",EDGE,"E55.1.0.4");Q2=makeQuery(id+"F22.boolean.opBoolean","SPLIT",EDGE,{"disambiguationData":[topologyDisambiguationEdgeConnected([makeQuery(id+"F2.opExtrude","SWEPT_FACE",FACE,{"disambiguationData":[OSD([subQ0])]})])],"derivedFrom":makeQuery(id+"F22.opExtrude","SWEPT_EDGE",EDGE,{"disambiguationData":[OSD([subQ0,sQuery(id+"F21.wireOp",EDGE,"E55.1.0.1"),subQ1])]})});}
            var Q3;
            {var subQ0=sQuery(id+"F1.wireOp",EDGE,"E17.3.0.1");var subQ1=sQuery(id+"F21.wireOp",EDGE,"E55.1.0.5");Q3=makeQuery(id+"F22.boolean.opBoolean","SPLIT",EDGE,{"disambiguationData":[topologyDisambiguationEdgeConnected([makeQuery(id+"F2.opExtrude","SWEPT_FACE",FACE,{"disambiguationData":[OSD([subQ0])]})])],"derivedFrom":makeQuery(id+"F22.opExtrude","SWEPT_EDGE",EDGE,{"disambiguationData":[OSD([subQ0,subQ1,sQuery(id+"F21.wireOp",EDGE,"E55.1.0.6")])]})});}
            var Q4;
            {var subQ0=sQuery(id+"F1.wireOp",EDGE,"E17.2.0.1");var subQ1=sQuery(id+"F21.wireOp",EDGE,"E55.2.0.5");Q4=makeQuery(id+"F22.boolean.opBoolean","SPLIT",EDGE,{"disambiguationData":[topologyDisambiguationEdgeConnected([makeQuery(id+"F2.opExtrude","SWEPT_FACE",FACE,{"disambiguationData":[OSD([subQ0])]})])],"derivedFrom":makeQuery(id+"F22.opExtrude","SWEPT_EDGE",EDGE,{"disambiguationData":[OSD([subQ0,subQ1,sQuery(id+"F21.wireOp",EDGE,"E55.2.0.6")])]})});}
            var Q5;
            {var subQ0=sQuery(id+"F1.wireOp",EDGE,"E17.2.0.0");var subQ1=sQuery(id+"F21.wireOp",EDGE,"E55.2.0.4");Q5=makeQuery(id+"F22.boolean.opBoolean","SPLIT",EDGE,{"disambiguationData":[topologyDisambiguationEdgeConnected([makeQuery(id+"F2.opExtrude","SWEPT_FACE",FACE,{"disambiguationData":[OSD([subQ0])]})])],"derivedFrom":makeQuery(id+"F22.opExtrude","SWEPT_EDGE",EDGE,{"disambiguationData":[OSD([subQ0,sQuery(id+"F21.wireOp",EDGE,"E55.2.0.1"),subQ1])]})});}
            var Q6;
            {var subQ0=sQuery(id+"F1.wireOp",EDGE,"E17.1.0.0");var subQ1=sQuery(id+"F21.wireOp",EDGE,"E55.3.0.4");Q6=makeQuery(id+"F22.boolean.opBoolean","SPLIT",EDGE,{"disambiguationData":[topologyDisambiguationEdgeConnected([makeQuery(id+"F2.opExtrude","SWEPT_FACE",FACE,{"disambiguationData":[OSD([subQ0])]})])],"derivedFrom":makeQuery(id+"F22.opExtrude","SWEPT_EDGE",EDGE,{"disambiguationData":[OSD([subQ0,sQuery(id+"F21.wireOp",EDGE,"E55.3.0.1"),subQ1])]})});}
            var Q7;
            {var subQ0=sQuery(id+"F1.wireOp",EDGE,"E16");var subQ1=sQuery(id+"F21.wireOp",EDGE,"E55.4.0.4");Q7=makeQuery(id+"F22.boolean.opBoolean","SPLIT",EDGE,{"disambiguationData":[topologyDisambiguationEdgeConnected([makeQuery(id+"F2.opExtrude","SWEPT_FACE",FACE,{"disambiguationData":[OSD([subQ0])]})])],"derivedFrom":makeQuery(id+"F22.opExtrude","SWEPT_EDGE",EDGE,{"disambiguationData":[OSD([subQ0,sQuery(id+"F21.wireOp",EDGE,"E55.4.0.1"),subQ1])]})});}
            var Q8;
            {var subQ0=sQuery(id+"F1.wireOp",EDGE,"E14");var subQ1=sQuery(id+"F21.wireOp",EDGE,"E55.4.0.5");Q8=makeQuery(id+"F22.boolean.opBoolean","SPLIT",EDGE,{"disambiguationData":[topologyDisambiguationEdgeConnected([makeQuery(id+"F2.opExtrude","SWEPT_FACE",FACE,{"disambiguationData":[OSD([subQ0])]})])],"derivedFrom":makeQuery(id+"F22.opExtrude","SWEPT_EDGE",EDGE,{"disambiguationData":[OSD([subQ0,subQ1,sQuery(id+"F21.wireOp",EDGE,"E55.4.0.6")])]})});}
            var Q9;
            {var subQ0=sQuery(id+"F1.wireOp",EDGE,"E17.1.0.1");var subQ1=sQuery(id+"F21.wireOp",EDGE,"E55.3.0.5");Q9=makeQuery(id+"F22.boolean.opBoolean","SPLIT",EDGE,{"disambiguationData":[topologyDisambiguationEdgeConnected([makeQuery(id+"F2.opExtrude","SWEPT_FACE",FACE,{"disambiguationData":[OSD([subQ0])]})])],"derivedFrom":makeQuery(id+"F22.opExtrude","SWEPT_EDGE",EDGE,{"disambiguationData":[OSD([subQ0,subQ1,sQuery(id+"F21.wireOp",EDGE,"E55.3.0.6")])]})});}
            chamfer(context, id + "F23", {"entities" : qUnion([Q0, Q1, Q2, Q3, Q4, Q5, Q6, Q7, Q8, Q9]), "width" : 1.12 * mm, "tangentPropagation" : true});
        }
    });
